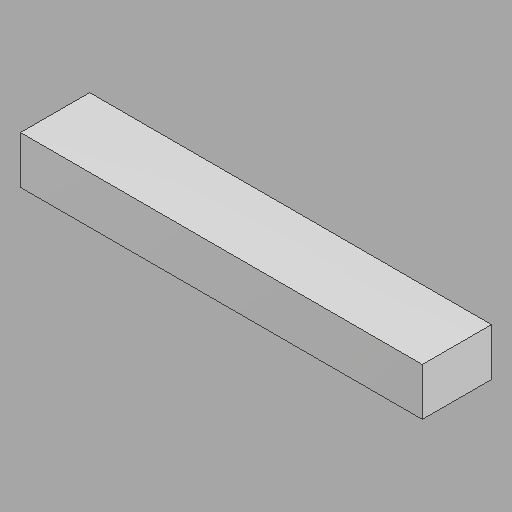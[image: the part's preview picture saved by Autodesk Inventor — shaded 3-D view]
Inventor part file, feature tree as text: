
AUTODESK INVENTOR PART (.ipt)
format: ipt  version: 2022.2 (Build 262287010, 287A)  size: 114,176 bytes
history: native  units: in
note: dims shown in document units (in); Inventor stores cm internally (conversion verified against a paired STEP export)
features: direct_edit x1, other x1, revolve x1
ambient origin geometry x8: Origin, YZ Plane, XZ Plane, XY Plane, X Axis, Y Axis, Z Axis, Center Point
bodies: Solid1 (feature_tree)
feature tree (3):
  direct_edit  "Direct Edit1"
  other  "L Vert rect jamb bottom_"
  revolve  "Rotate1"  Angle=90.0deg
